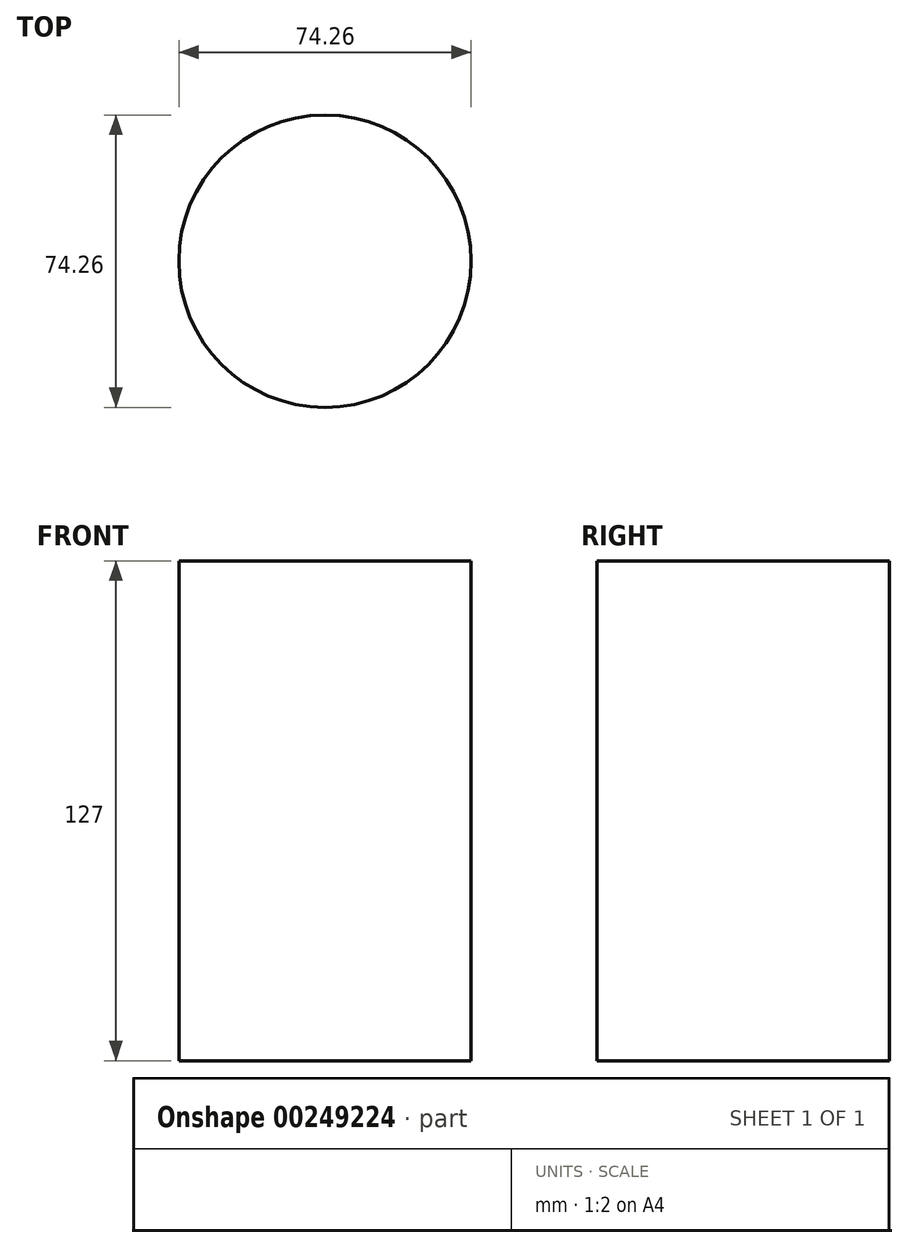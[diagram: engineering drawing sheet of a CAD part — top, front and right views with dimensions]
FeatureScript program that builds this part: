
annotation { "Feature Type Name" : "Feature", "Feature Type Description" : "" }
export const myFeature = defineFeature(function(context is Context, id is Id, definition is map)
    precondition{}
    {
        {
            var Q0;
            Q0=qCreatedBy(makeId("Top.planeOp"),FACE);
            var sketch = newSketch(context, id + "F0", { "sketchPlane" : qUnion([Q0])});
            skCircle(sketch, "E0", {"center": v(0, 0) * mm, "radius": 37.13 * mm});
            skSolve(sketch);
        }
        {
            var Q0;
            Q0 = qSketchRegion(id + "F0", true);
            extrude(context, id + "F1", {"entities" : qUnion([Q0]), "depth" : 127 * mm});
        }
    });
